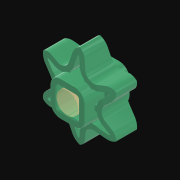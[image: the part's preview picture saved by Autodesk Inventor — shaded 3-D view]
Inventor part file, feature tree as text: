
AUTODESK INVENTOR PART (.ipt)
format: ipt  version: 2021 (Build 250183000, 183)  size: 1,061,376 bytes
history: native  units: in
note: dims shown in document units (in); Inventor stores cm internally (conversion verified against a paired STEP export)
features: sketch x1, other x1, fillet x1, extrude x1
ambient origin geometry x8: Origin, YZ Plane, XZ Plane, XY Plane, X Axis, Y Axis, Z Axis, Center Point
bodies: Solid1 (feature_tree)
feature tree (4):
  sketch  "Sketch1"
  other  "Srf1"
  fillet  "Fillet4"  Radius=0.3937in
  extrude  "ExtrusionSrf1"  [1 undecoded]
note: 1 required parameter value undecoded (feature->parameter linkage not recoverable at this tier; creation-order binding heuristic only, values carry confidence <= 0.55)
